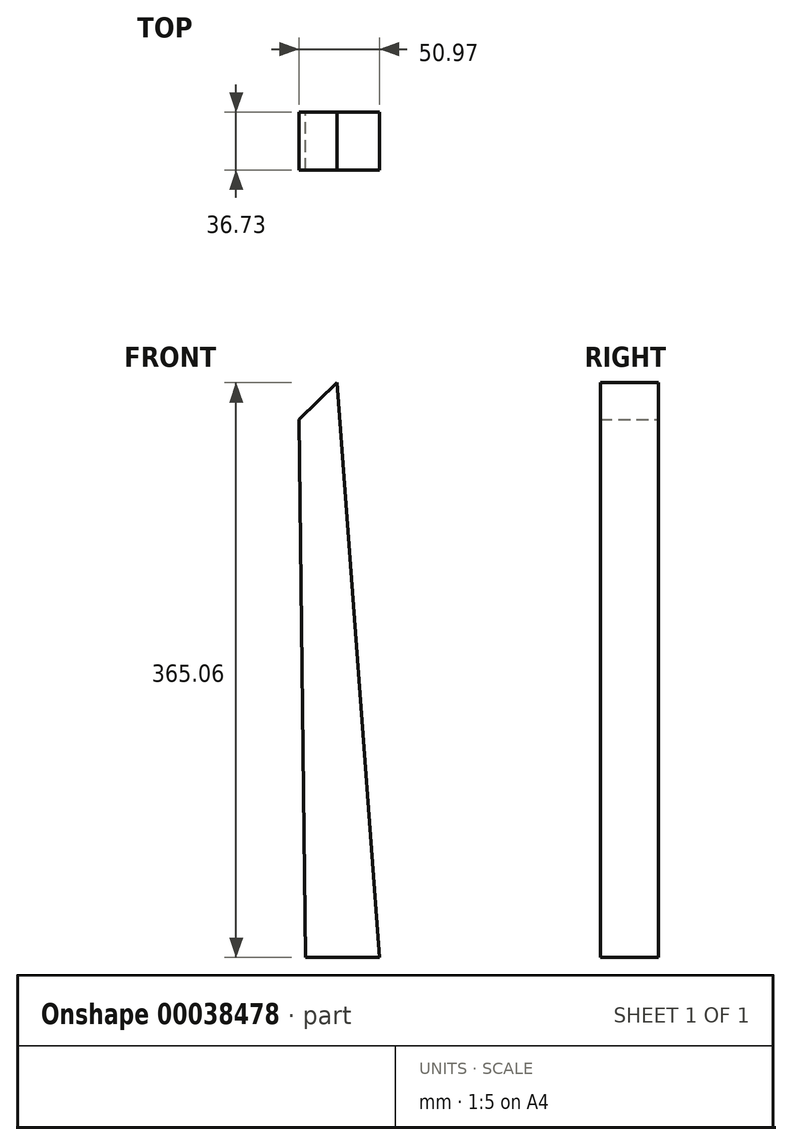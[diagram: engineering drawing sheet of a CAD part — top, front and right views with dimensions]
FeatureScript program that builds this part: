
annotation { "Feature Type Name" : "Feature", "Feature Type Description" : "" }
export const myFeature = defineFeature(function(context is Context, id is Id, definition is map)
    precondition{}
    {
        {
            var Q0;
            Q0=qCreatedBy(makeId("Front.planeOp"),FACE);
            var sketch = newSketch(context, id + "F0", { "sketchPlane" : qUnion([Q0])});
            skLineSegment(sketch, "E0", {"start": v(36.7, 140.47) * mm, "end": v(60.8, 163.89) * mm});
            skLineSegment(sketch, "E1", {"start": v(60.8, 163.89) * mm, "end": v(87.67, -201.17) * mm});
            skLineSegment(sketch, "E2", {"start": v(87.67, -201.17) * mm, "end": v(40.83, -201.17) * mm});
            skLineSegment(sketch, "E3", {"start": v(40.83, -201.17) * mm, "end": v(36.7, 140.47) * mm});
            skSolve(sketch);
        }
        {
            var Q0;
            Q0=makeQuery(id+"F0.imprint","IMPRINT",FACE,{"disambiguationData":[TD([[makeQuery(id+"F0.imprint","IMPRINT",EDGE,{"derivedFrom":sQuery(id+"F0.wireOp",EDGE,"E0")}),-1.0]])]});
            extrude(context, id + "F1", {"entities" : qUnion([Q0]), "depth" : 36.73 * mm});
        }
    });
